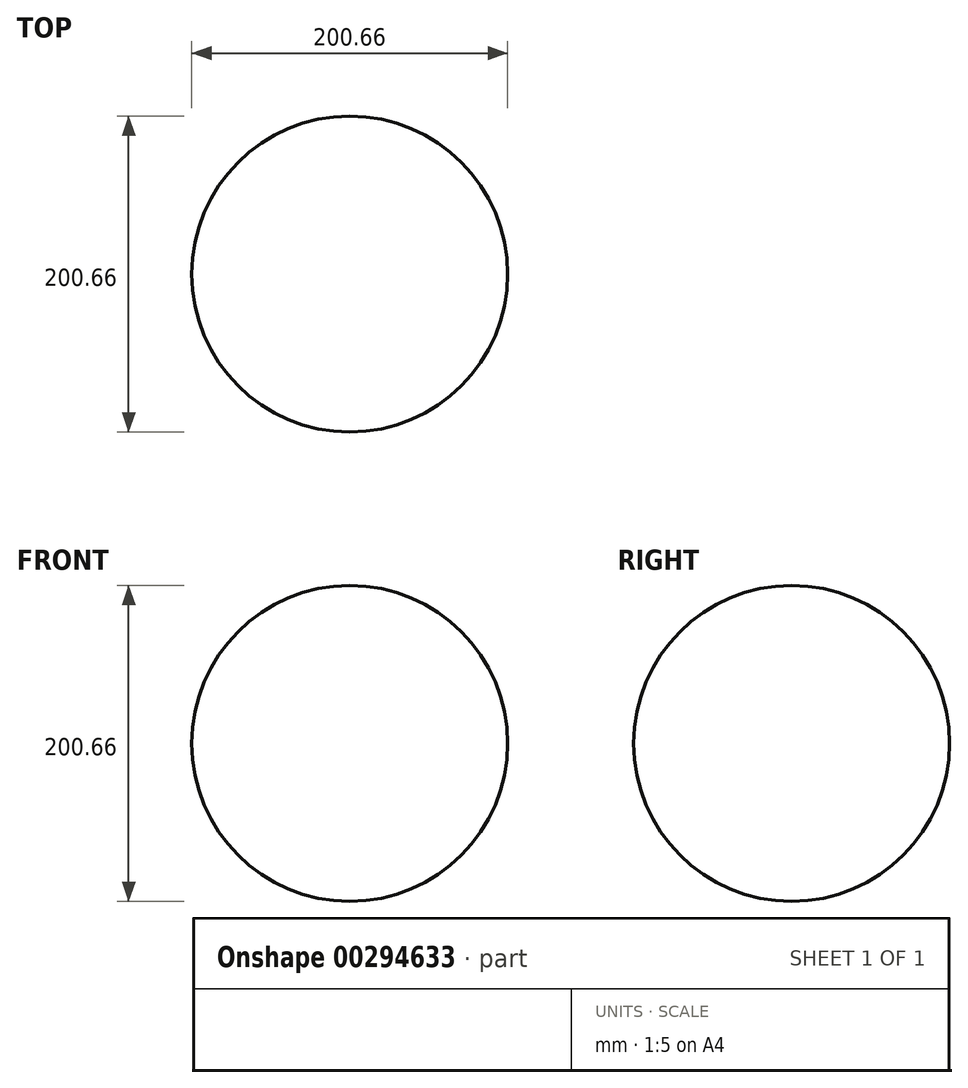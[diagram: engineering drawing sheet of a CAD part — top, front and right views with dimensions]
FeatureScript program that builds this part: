
annotation { "Feature Type Name" : "Feature", "Feature Type Description" : "" }
export const myFeature = defineFeature(function(context is Context, id is Id, definition is map)
    precondition{}
    {
        {
            var Q0;
            Q0=qCreatedBy(makeId("Front.planeOp"),FACE);
            var sketch = newSketch(context, id + "F0", { "sketchPlane" : qUnion([Q0])});
            skArc(sketch, "E0", {"start": v(0, -100.33) * mm, "mid": v(100.33, 0) * mm, "end": v(0, 100.33) * mm});
            skLineSegment(sketch, "E1", {"start": v(0, 100.33) * mm, "end": v(0, -100.33) * mm});
            skSolve(sketch);
        }
        {
            var Q0;
            Q0 = qSketchRegion(id + "F0", true);
            var Q1;
            Q1=sQuery(id+"F0.wireOp",EDGE,"E1");
            revolve(context, id + "F1", {"entities" : qUnion([Q0]), "axis" : qUnion([Q1]), "revolveType" : RevolveType.FULL});
        }
    });
